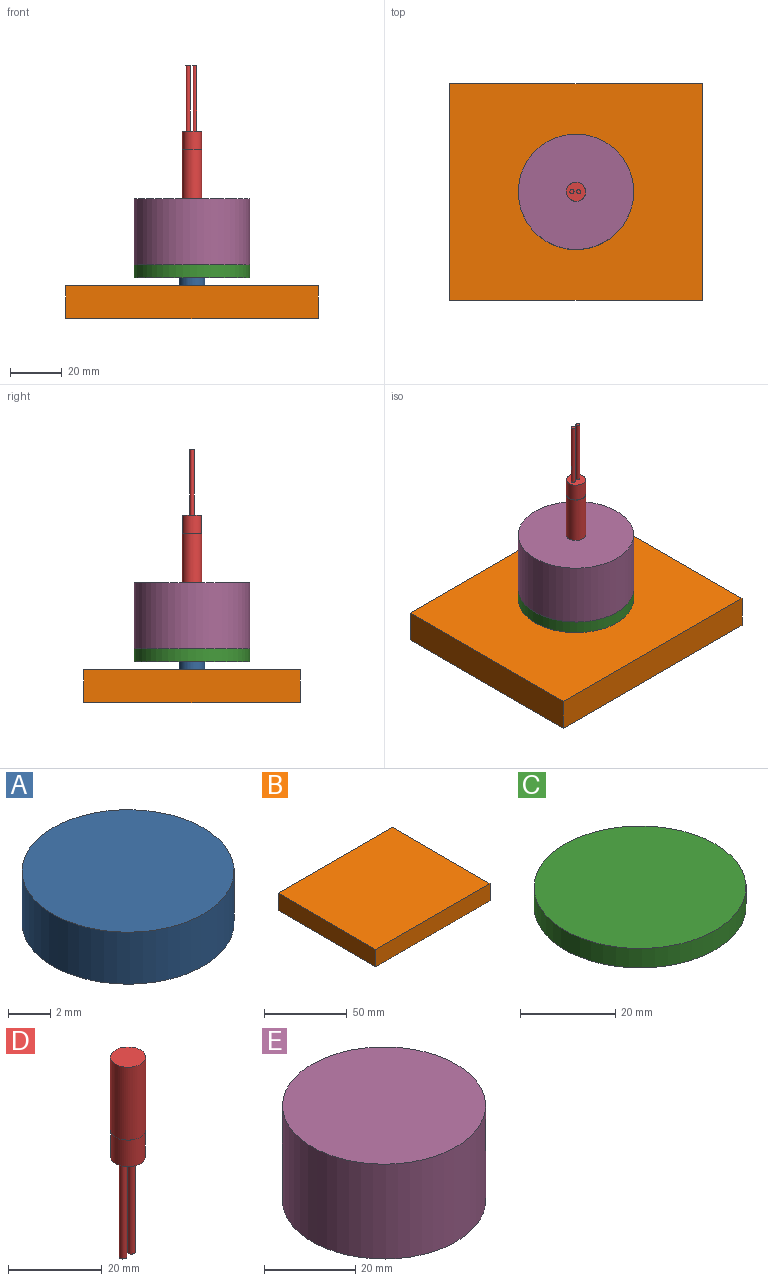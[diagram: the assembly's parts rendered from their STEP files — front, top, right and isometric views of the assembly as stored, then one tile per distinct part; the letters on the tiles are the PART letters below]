
ASSEMBLY  parts=5 mates=7
PART A: 3 faces, bbox 10x10x3 mm
  f0: cylinder r=5mm len=10mm, axis (0,0,-1), area 94.2mm2, adj f1,f2
  f1: plane 10x10mm, normal (0,0,1), area 78.5mm2, adj f0
  f2: plane 10x10mm, normal (0,0,-1), area 78.5mm2, adj f0
PART B: 6 faces, bbox 97.3x83.5x12.7 mm
  f0: plane 97.28x12.7mm, normal (0,1,0), area 1235.4mm2, adj f1,f3,f4,f5
  f1: plane 83.49x12.7mm, normal (-1,0,0), area 1060.3mm2, adj f0,f2,f4,f5
  f2: plane 97.28x12.7mm, normal (0,-1,0), area 1235.4mm2, adj f1,f3,f4,f5
  f3: plane 83.49x12.7mm, normal (1,0,0), area 1060.3mm2, adj f0,f2,f4,f5
  f4: plane 97.28x83.49mm, normal (0,0,1), area 8121.8mm2, adj f0,f1,f2,f3
  f5: plane 97.28x83.49mm, normal (0,0,-1), area 8121.8mm2, adj f0,f1,f2,f3
PART C: 3 faces, bbox 44.5x44.5x5 mm
  f0: cylinder r=22.23mm len=44.45mm, axis (0,0,-1), area 698.2mm2, adj f1,f2
  f1: plane 44.45x44.45mm, normal (0,0,1), area 1551.8mm2, adj f0
  f2: plane 44.45x44.45mm, normal (0,0,-1), area 1551.8mm2, adj f0
PART D: 9 faces, bbox 7.5x7.5x51.4 mm
  f0: cylinder r=3.68mm len=7.37mm, axis (0,0,1), area 161.6mm2, adj f1,f8
  f1: plane 7.37x7.37mm, normal (0,0,-1), area 38.7mm2, adj f0,f2,f4
  f2: cylinder r=0.79mm len=25.4mm, axis (0,0,1), area 125.7mm2, adj f1,f3
  f3: plane 1.57x1.57mm, normal (0,0,-1), area 1.9mm2, adj f2
  f4: cylinder r=0.79mm len=25.4mm, axis (0,0,1), area 125.7mm2, adj f1,f5
  f5: plane 1.57x1.57mm, normal (0,0,-1), area 1.9mm2, adj f4
  f6: cylinder r=3.75mm len=19.05mm, axis (0,0,-1), area 448.4mm2, adj f7,f8
  f7: plane 7.49x7.49mm, normal (0,0,1), area 44.1mm2, adj f6
  f8: plane 7.49x7.49mm, normal (0,0,-1), area 1.5mm2, adj f0,f6
PART E: 3 faces, bbox 44.5x44.5x25.4 mm
  f0: cylinder r=22.23mm len=44.45mm, axis (0,0,-1), area 3547mm2, adj f1,f2
  f1: plane 44.45x44.45mm, normal (0,0,1), area 1551.8mm2, adj f0
  f2: plane 44.45x44.45mm, normal (0,0,-1), area 1551.8mm2, adj f0
PLACE A t=(-25.3,-16.89,2.93)mm
PLACE B t=(-27.26,3.06,-9.77)mm fixed
PLACE C t=(-25.3,-16.89,5.93)mm
PLACE D rot(axis=(1,0,0),180deg) t=(-25.3,-16.89,55.38)mm
PLACE E t=(-25.3,-16.89,10.93)mm
MATE planar C.f0 <-> E.f0  axis (0,0,1) through (-25.3,-16.89,10.93)mm
MATE cylindrical C.f0 <-> E.f0  axis (0,0,-1) through (-25.3,-16.89,8.43)mm
MATE planar D.f0 <-> E.f0  axis (0,0,1) through (-25.3,-16.89,36.33)mm
MATE cylindrical D.f0 <-> E.f0  axis (0,0,1) through (-25.3,-16.89,45.85)mm
MATE planar A.f0 <-> C.f0  axis (0,0,1) through (-25.3,-16.89,5.93)mm
MATE planar A.f0 <-> B.f4  axis (0,0,-1) through (-25.3,-16.89,2.93)mm
MATE cylindrical A.f0 <-> C.f0  axis (0,0,-1) through (-25.3,-16.89,5.93)mm
